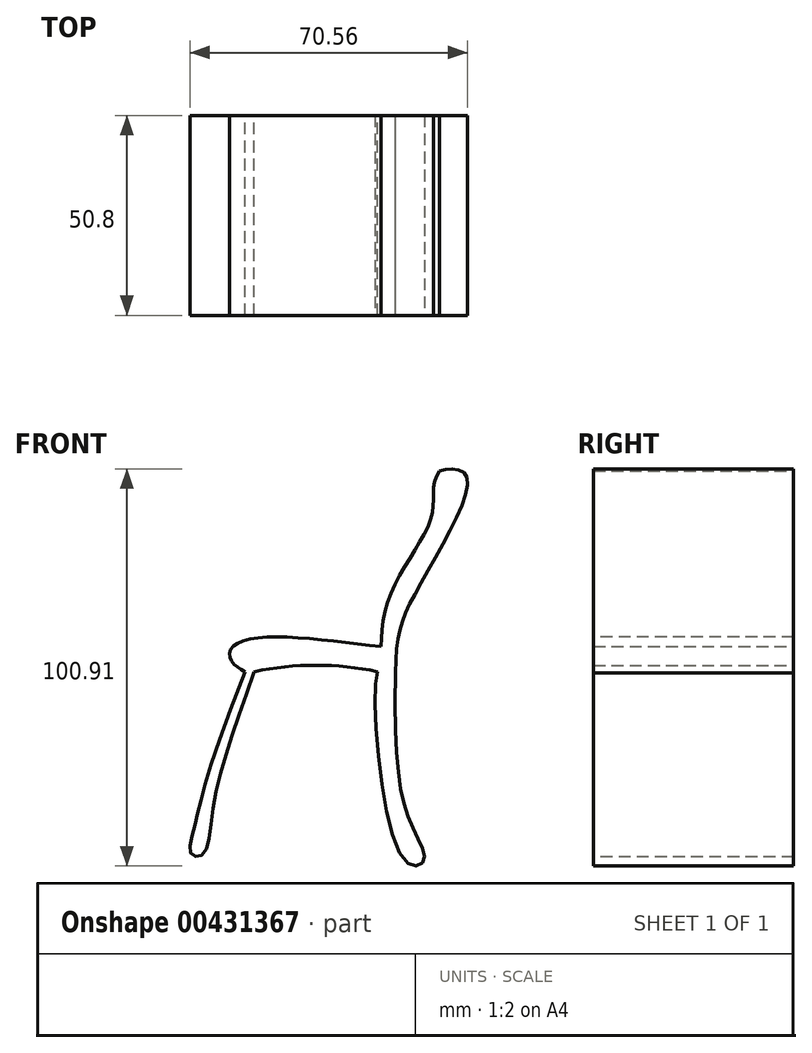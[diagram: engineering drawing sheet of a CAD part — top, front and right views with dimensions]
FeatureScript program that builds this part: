
annotation { "Feature Type Name" : "Feature", "Feature Type Description" : "" }
export const myFeature = defineFeature(function(context is Context, id is Id, definition is map)
    precondition{}
    {
        {
            var Q0;
            Q0=qCreatedBy(makeId("Front.planeOp"),FACE);
            var sketch = newSketch(context, id + "F0", { "sketchPlane" : qUnion([Q0])});
            skLineSegment(sketch, "E0", {"start": v(5.16, 27.8) * mm, "end": v(0.64, 28.1) * mm});
            skArc(sketch, "E1", {"start": v(0.64, 28.1) * mm, "mid": v(-15.02, 29.75) * mm, "end": v(-30.68, 28.1) * mm});
            skFitSpline(sketch, "E2", {"points": [v(-30.68, 28.1) * mm, v(-40.96, -5.45) * mm, v(-43.79, -18.42) * mm, v(-46.62, -18.27) * mm, v(-46.02, -11.86) * mm, v(-33.06, 28.1) * mm], "startDerivative": vector(-44.98, -132.57) * mm, "endDerivative": vector(95.15, 242.43) * mm});
            skLineSegment(sketch, "E3", {"start": v(-33.06, 28.1) * mm, "end": v(-30.68, 28.1) * mm});
            skFitSpline(sketch, "E4", {"points": [v(5.16, 27.8) * mm, v(10.42, 48.32) * mm, v(23.21, 77.92) * mm, v(16.44, 79.15) * mm], "startDerivative": vector(2.54, 81.63) * mm, "endDerivative": vector(-30.03, -10.12) * mm});
            skFitSpline(sketch, "E5", {"points": [v(16.44, 79.15) * mm, v(14.5, 68) * mm, v(2.98, 45.13) * mm, v(0.64, 28.1) * mm], "startDerivative": vector(-29.82, -37.78) * mm, "endDerivative": vector(-12.67, -24.17) * mm});
            skFitSpline(sketch, "E6", {"points": [v(5.16, 27.8) * mm, v(9.29, -10.94) * mm, v(12.41, -19.88) * mm, v(7.65, -20.03) * mm, v(0.64, 28.1) * mm], "startDerivative": vector(-1.7, -191.59) * mm, "endDerivative": vector(15.19, 47.59) * mm});
            skFitSpline(sketch, "E7", {"points": [v(-33.06, 28.1) * mm, v(-36.25, 30.6) * mm, v(-36.55, 33.88) * mm, v(-27.76, 36.86) * mm, v(1.52, 34.48) * mm], "startDerivative": vector(-22.47, 13.31) * mm, "endDerivative": vector(66.43, -7.13) * mm});
            skSolve(sketch);
        }
        {
            var Q0;
            {var subQ0=sQuery(id+"F0.wireOp",EDGE,"E1");Q0=makeQuery(id+"F0.imprint","IMPRINT",FACE,{"disambiguationData":[TD([[makeQuery(id+"F0.imprint","IMPRINT",EDGE,{"derivedFrom":subQ0}),-1.0]])]});}
            var Q1;
            {var subQ0=sQuery(id+"F0.wireOp",EDGE,"E0");Q1=makeQuery(id+"F0.imprint","IMPRINT",FACE,{"disambiguationData":[TD([[makeQuery(id+"F0.imprint","IMPRINT",EDGE,{"derivedFrom":subQ0}),-1.0]])]});}
            var Q2;
            Q2=makeQuery(id+"F0.imprint","IMPRINT",FACE,{"disambiguationData":[TD([[makeQuery(id+"F0.imprint","IMPRINT",EDGE,{"derivedFrom":sQuery(id+"F0.wireOp",EDGE,"E0")}),1.0]])]});
            var Q3;
            Q3=makeQuery(id+"F0.imprint","IMPRINT",FACE,{"disambiguationData":[TD([[makeQuery(id+"F0.imprint","IMPRINT",EDGE,{"derivedFrom":sQuery(id+"F0.wireOp",EDGE,"E2")}),-1.0]])]});
            extrude(context, id + "F1", {"entities" : qUnion([Q0, Q1, Q2, Q3]), "depth" : 50.8 * mm});
        }
    });
